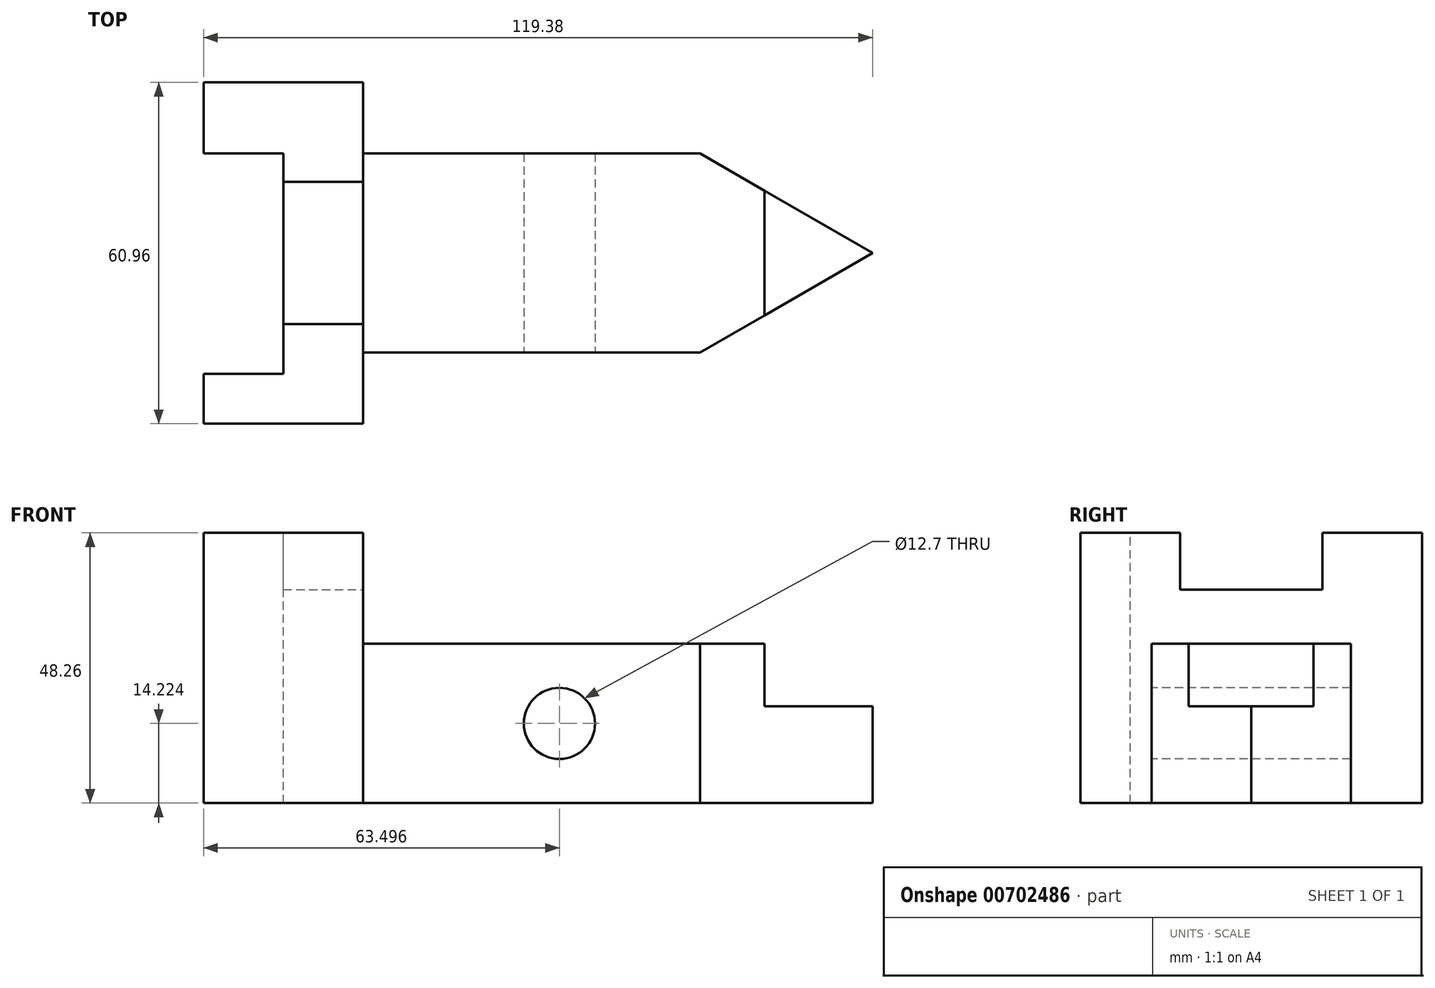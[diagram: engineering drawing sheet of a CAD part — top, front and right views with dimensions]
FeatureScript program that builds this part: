
annotation { "Feature Type Name" : "Feature", "Feature Type Description" : "" }
export const myFeature = defineFeature(function(context is Context, id is Id, definition is map)
    precondition{}
    {
        {
            var Q0;
            Q0=qCreatedBy(makeId("Top.planeOp"),FACE);
            var sketch = newSketch(context, id + "F0", { "sketchPlane" : qUnion([Q0])});
            skLineSegment(sketch, "E0.bottom", {"start": v(14.22, 30.48) * mm, "end": v(-14.22, 30.48) * mm});
            skLineSegment(sketch, "E0.top", {"start": v(14.22, -30.48) * mm, "end": v(-14.22, -30.48) * mm});
            skLineSegment(sketch, "E0.left", {"start": v(14.22, 30.48) * mm, "end": v(14.22, -30.48) * mm});
            skLineSegment(sketch, "E0.right", {"start": v(-14.22, 30.48) * mm, "end": v(-14.22, -30.48) * mm});
            skPoint(sketch, "E0.middle", {"position": v(0, 0) * mm});
            skSolve(sketch);
        }
        {
            var Q0;
            Q0=makeQuery(id+"F0.imprint","IMPRINT",FACE,{"disambiguationData":[TD([[makeQuery(id+"F0.imprint","IMPRINT",EDGE,{"derivedFrom":sQuery(id+"F0.wireOp",EDGE,"E0.bottom")}),1.0]])]});
            extrude(context, id + "F1", {"entities" : qUnion([Q0]), "depth" : 48.26 * mm});
        }
        {
            var Q0;
            Q0=makeQuery(id+"F1.opExtrude","SWEPT_FACE",FACE,{"disambiguationData":[OSD([sQuery(id+"F0.wireOp",EDGE,"E0.left")])]});
            var sketch = newSketch(context, id + "F2", { "sketchPlane" : qUnion([Q0])});
            skLineSegment(sketch, "E1.bottom", {"start": v(-12.7, 48.26) * mm, "end": v(12.7, 48.26) * mm});
            skLineSegment(sketch, "E1.top", {"start": v(-12.7, 38.1) * mm, "end": v(12.7, 38.1) * mm});
            skLineSegment(sketch, "E1.left", {"start": v(-12.7, 48.26) * mm, "end": v(-12.7, 38.1) * mm});
            skLineSegment(sketch, "E1.right", {"start": v(12.7, 48.26) * mm, "end": v(12.7, 38.1) * mm});
            skSolve(sketch);
        }
        {
            var Q0;
            Q0=qSketchRegion(id+"F2",true);
            extrude(context, id + "F3", {"entities" : qUnion([Q0]), "operationType" : NewBodyOperationType.REMOVE, "endBound" : BoundingType.THROUGH_ALL, "oppositeDirection" : true, "depth" : 25.4 * mm});
        }
        {
            var Q0;
            {var subQ0=sQuery(id+"F0.wireOp",EDGE,"E0.top");var subQ1=sQuery(id+"F0.wireOp",EDGE,"E0.left");var subQ2=sQuery(id+"F0.wireOp",EDGE,"E0.right");Q0=makeQuery(id+"F3.boolean.opBoolean","SPLIT",FACE,{"disambiguationData":[TD([makeQuery(id+"F1.opExtrude","SWEPT_FACE",FACE,{"disambiguationData":[OSD([subQ0])]})])],"derivedFrom":makeQuery(id+"F1.opExtrude","CAP_FACE",FACE,{"disambiguationData":[OSD([sQuery(id+"F0.wireOp",EDGE,"E0.bottom"),subQ0,subQ1,subQ2])],"isStart":false})});}
            var sketch = newSketch(context, id + "F4", { "sketchPlane" : qUnion([Q0])});
            skLineSegment(sketch, "E2.bottom", {"start": v(-14.22, -21.6) * mm, "end": v(0, -21.6) * mm});
            skLineSegment(sketch, "E2.top", {"start": v(-14.22, 17.78) * mm, "end": v(0, 17.78) * mm});
            skLineSegment(sketch, "E2.left", {"start": v(-14.22, -21.6) * mm, "end": v(-14.22, 17.78) * mm});
            skLineSegment(sketch, "E2.right", {"start": v(0, -21.6) * mm, "end": v(0, 17.78) * mm});
            skSolve(sketch);
        }
        {
            var Q0;
            Q0=qSketchRegion(id+"F4",true);
            extrude(context, id + "F5", {"entities" : qUnion([Q0]), "operationType" : NewBodyOperationType.REMOVE, "endBound" : BoundingType.THROUGH_ALL, "oppositeDirection" : true, "depth" : 25.4 * mm});
        }
        {
            var Q0;
            Q0=makeQuery(id+"F1.opExtrude","SWEPT_FACE",FACE,{"disambiguationData":[OSD([sQuery(id+"F0.wireOp",EDGE,"E0.left")])]});
            var sketch = newSketch(context, id + "F6", { "sketchPlane" : qUnion([Q0])});
            skLineSegment(sketch, "E3.bottom", {"start": v(-17.78, 0) * mm, "end": v(17.78, 0) * mm});
            skLineSegment(sketch, "E3.top", {"start": v(-17.78, 28.45) * mm, "end": v(17.78, 28.45) * mm});
            skLineSegment(sketch, "E3.left", {"start": v(-17.78, 0) * mm, "end": v(-17.78, 28.45) * mm});
            skLineSegment(sketch, "E3.right", {"start": v(17.78, 0) * mm, "end": v(17.78, 28.45) * mm});
            skSolve(sketch);
        }
        {
            var Q0;
            Q0=qSketchRegion(id+"F6",true);
            extrude(context, id + "F7", {"entities" : qUnion([Q0]), "operationType" : NewBodyOperationType.ADD, "depth" : 90.93 * mm});
        }
        {
            var Q0;
            Q0=makeQuery(id+"F7.opExtrude","SWEPT_FACE",FACE,{"disambiguationData":[OSD([sQuery(id+"F6.wireOp",EDGE,"E3.left")])]});
            var sketch = newSketch(context, id + "F8", { "sketchPlane" : qUnion([Q0])});
            skLineSegment(sketch, "E4.bottom", {"start": v(105.16, 28.45) * mm, "end": v(85.85, 28.45) * mm});
            skLineSegment(sketch, "E4.top", {"start": v(105.16, 17.27) * mm, "end": v(85.85, 17.27) * mm});
            skLineSegment(sketch, "E4.left", {"start": v(105.16, 28.45) * mm, "end": v(105.16, 17.27) * mm});
            skLineSegment(sketch, "E4.right", {"start": v(85.85, 28.45) * mm, "end": v(85.85, 17.27) * mm});
            skSolve(sketch);
        }
        {
            var Q0;
            Q0=qSketchRegion(id+"F8",true);
            extrude(context, id + "F9", {"entities" : qUnion([Q0]), "operationType" : NewBodyOperationType.REMOVE, "endBound" : BoundingType.THROUGH_ALL, "oppositeDirection" : true, "depth" : 25.4 * mm});
        }
        {
            var Q0;
            Q0=makeQuery(id+"F7.boolean.opBoolean","MERGE",FACE,{"derivedFrom":[makeQuery(id+"F1.opExtrude","CAP_FACE",FACE,{"disambiguationData":[OSD([sQuery(id+"F0.wireOp",EDGE,"E0.bottom"),sQuery(id+"F0.wireOp",EDGE,"E0.top"),sQuery(id+"F0.wireOp",EDGE,"E0.left"),sQuery(id+"F0.wireOp",EDGE,"E0.right")])],"isStart":true}),makeQuery(id+"F7.opExtrude","SWEPT_FACE",FACE,{"disambiguationData":[OSD([sQuery(id+"F6.wireOp",EDGE,"E3.bottom")])]})]});
            var sketch = newSketch(context, id + "F10", { "sketchPlane" : qUnion([Q0])});
            skLineSegment(sketch, "E5", {"start": v(105.16, 0) * mm, "end": v(74.36, 17.78) * mm});
            skLineSegment(sketch, "E6", {"start": v(74.36, 17.78) * mm, "end": v(105.16, 17.78) * mm});
            skLineSegment(sketch, "E7", {"start": v(105.16, 17.78) * mm, "end": v(105.16, -17.78) * mm});
            skLineSegment(sketch, "E8", {"start": v(105.16, -17.78) * mm, "end": v(74.36, -17.78) * mm});
            skLineSegment(sketch, "E9", {"start": v(74.36, -17.78) * mm, "end": v(105.16, 0) * mm});
            skSolve(sketch);
        }
        {
            var Q0;
            Q0=qSketchRegion(id+"F10",true);
            extrude(context, id + "F11", {"entities" : qUnion([Q0]), "operationType" : NewBodyOperationType.REMOVE, "endBound" : BoundingType.THROUGH_ALL, "oppositeDirection" : true, "depth" : 25.4 * mm});
        }
        {
            var Q0;
            Q0=makeQuery(id+"F7.opExtrude","SWEPT_FACE",FACE,{"disambiguationData":[OSD([sQuery(id+"F6.wireOp",EDGE,"E3.left")])]});
            var sketch = newSketch(context, id + "F12", { "sketchPlane" : qUnion([Q0])});
            skCircle(sketch, "E10", {"center": v(49.28, 14.22) * mm, "radius": 6.35 * mm});
            skSolve(sketch);
        }
        {
            var Q0;
            Q0=qSketchRegion(id+"F12",true);
            extrude(context, id + "F13", {"entities" : qUnion([Q0]), "operationType" : NewBodyOperationType.REMOVE, "endBound" : BoundingType.THROUGH_ALL, "oppositeDirection" : true, "depth" : 25.4 * mm});
        }
    });
